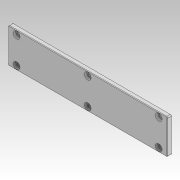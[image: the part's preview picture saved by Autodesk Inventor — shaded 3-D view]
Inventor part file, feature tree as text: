
AUTODESK INVENTOR PART (.ipt)
format: ipt  version: 2020 (Build 240168000, 168)  size: 144,896 bytes
history: native  units: mm
features: extrude x2, sketch x2, fillet x1
ambient origin geometry x8: Origin, YZ Plane, XZ Plane, XY Plane, X Axis, Y Axis, Z Axis, Center Point
bodies: Solid1 (feature_tree)
feature tree (5):
  extrude  "Extrusion1"  Depth=31.5mm
  extrude  "Extrusion2"  Depth=12.0mm
  fillet  "Fillet1"  Radius=3.5mm
  sketch  "Sketch1"  dims[d0=144.0mm d1=31.5mm]
  sketch  "Sketch2"  dims[d2=64.25mm d3=12.0mm d4=3.5mm d5=1.0mm d6=4.0mm d7=0.0mm d8=6.0mm d9=2.2mm d10=0.0mm d11=0.5mm]
